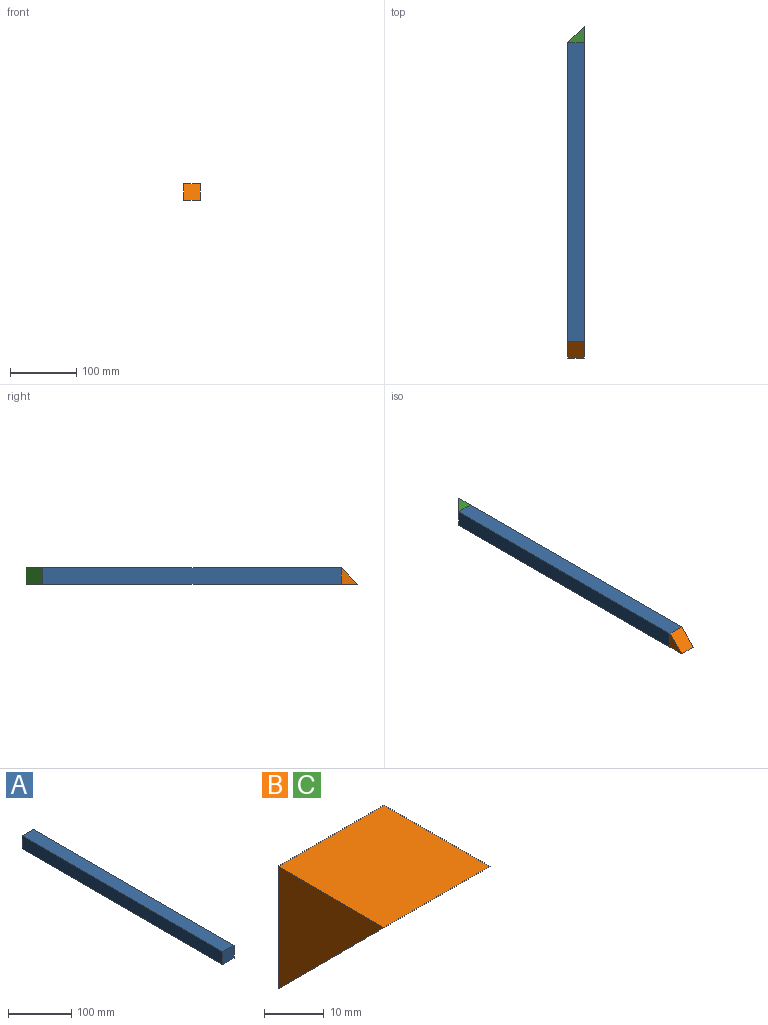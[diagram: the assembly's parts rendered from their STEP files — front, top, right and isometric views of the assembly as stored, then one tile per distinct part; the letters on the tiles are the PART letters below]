
ASSEMBLY  parts=3 mates=2
PART A: 6 faces, bbox 25x450x25 mm
  f0: plane 450x25mm, normal (0,0,1), area 11250mm2, adj f1,f3,f4,f5
  f1: plane 450x25mm, normal (-1,0,0), area 11250mm2, adj f0,f2,f4,f5
  f2: plane 450x25mm, normal (0,0,-1), area 11250mm2, adj f1,f3,f4,f5
  f3: plane 450x25mm, normal (1,0,0), area 11250mm2, adj f0,f2,f4,f5
  f4: plane 25x25mm, normal (0,-1,0), area 625mm2, adj f0,f1,f2,f3
  f5: plane 25x25mm, normal (0,1,0), area 625mm2, adj f0,f1,f2,f3
PART B: 5 faces, bbox 25x25x25 mm
  f0: plane 25x25mm, normal (-1,0,0), area 312.5mm2, adj f2,f3,f4
  f1: plane 25x25mm, normal (1,0,0), area 312.5mm2, adj f2,f3,f4
  f2: plane 25x25mm, normal (0,0,1), area 625mm2, adj f0,f1,f3,f4
  f3: plane 25x25mm, normal (0,1,0), area 625mm2, adj f0,f1,f2,f4
  f4: plane 25x25mm, normal (0,-0.71,-0.71), area 883.9mm2, adj f0,f1,f2,f3
PART C: same geometry as B
PLACE A t=(-137.4,116.7,-80.96)mm
PLACE B rot(axis=(0,1,0),180deg) t=(-137.4,-333.3,-80.96)mm
PLACE C rot(axis=(0.71,0,0.71),180deg) t=(-137.4,116.7,-80.96)mm
MATE fastened C.f3 <-> A.f5  axis (0,-1,0) through (-137.4,116.7,-80.96)mm
MATE fastened B.f3 <-> A.f4  axis (0,1,0) through (-137.4,-333.3,-80.96)mm
